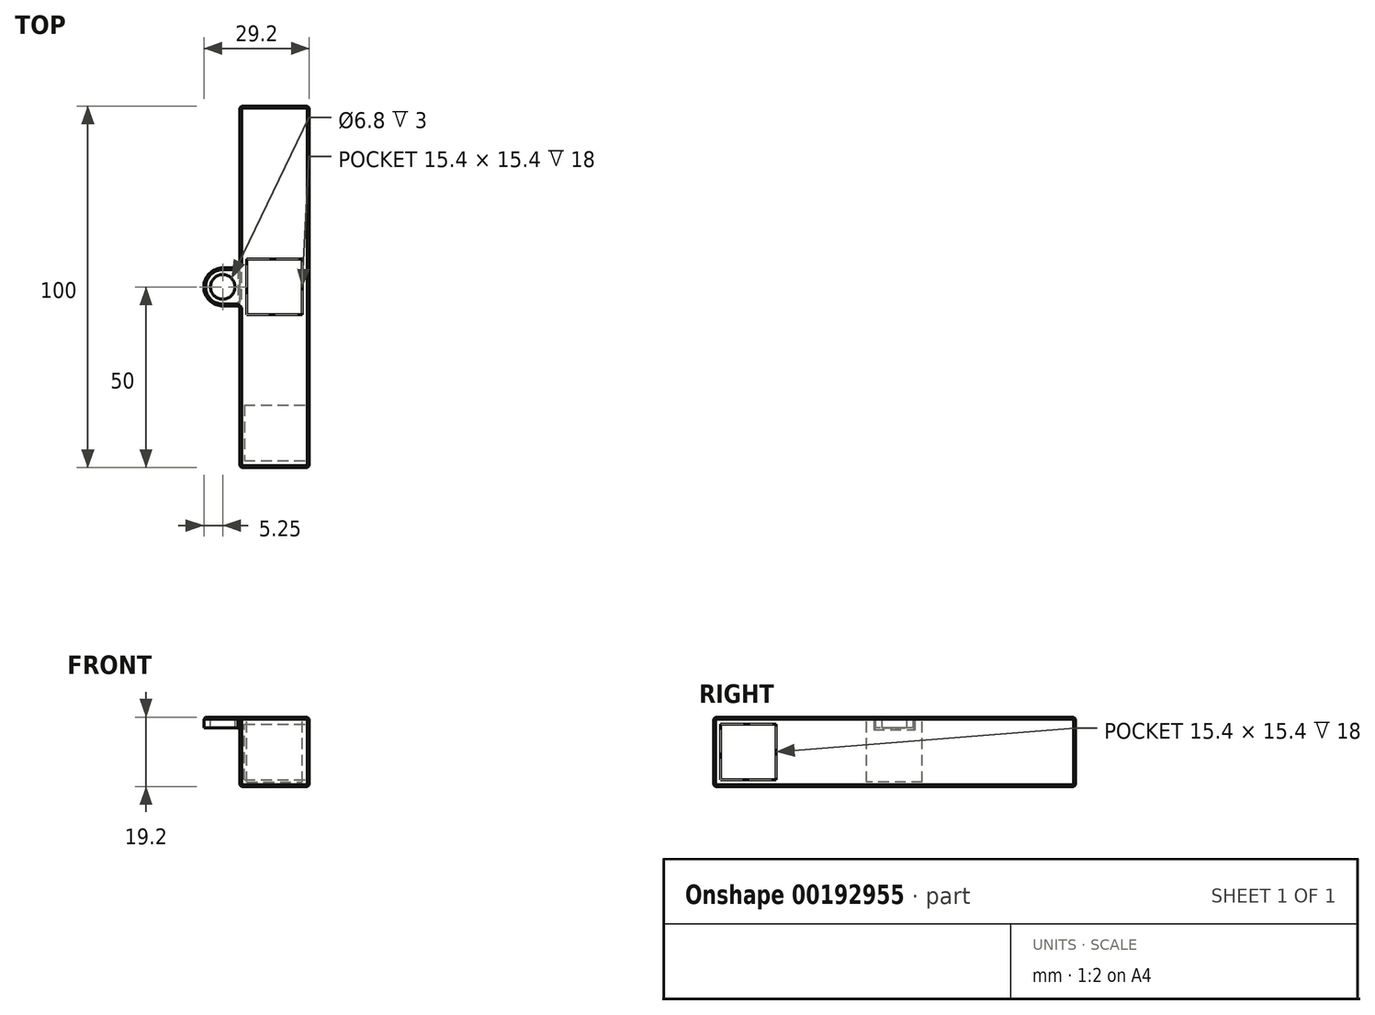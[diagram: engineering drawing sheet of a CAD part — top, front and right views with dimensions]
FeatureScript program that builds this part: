
annotation { "Feature Type Name" : "Feature", "Feature Type Description" : "" }
export const myFeature = defineFeature(function(context is Context, id is Id, definition is map)
    precondition{}
    {
        {
            var Q0;
            Q0=qCreatedBy(makeId("Top.planeOp"),FACE);
            var sketch = newSketch(context, id + "F0", { "sketchPlane" : qUnion([Q0])});
            skLineSegment(sketch, "E0.bottom", {"start": v(9.6, -50) * mm, "end": v(-9.6, -50) * mm});
            skLineSegment(sketch, "E0.top", {"start": v(9.6, 50) * mm, "end": v(-9.6, 50) * mm});
            skLineSegment(sketch, "E0.left", {"start": v(9.6, -50) * mm, "end": v(9.6, 50) * mm});
            skLineSegment(sketch, "E0.right", {"start": v(-9.6, -50) * mm, "end": v(-9.6, 50) * mm});
            skPoint(sketch, "E0.middle", {"position": v(0, 0) * mm});
            skSolve(sketch);
        }
        {
            var Q0;
            Q0=qSketchRegion(id+"F0",true);
            extrude(context, id + "F1", {"entities" : qUnion([Q0]), "depth" : 19.2 * mm});
        }
        {
            var Q0;
            Q0=makeQuery(id+"F1.opExtrude","SWEPT_FACE",FACE,{"disambiguationData":[OSD([sQuery(id+"F0.wireOp",EDGE,"E0.left")])]});
            var sketch = newSketch(context, id + "F2", { "sketchPlane" : qUnion([Q0])});
            skLineSegment(sketch, "E1.bottom", {"start": v(-32.7, 1.9) * mm, "end": v(-48.1, 1.9) * mm});
            skLineSegment(sketch, "E1.top", {"start": v(-32.7, 17.3) * mm, "end": v(-48.1, 17.3) * mm});
            skLineSegment(sketch, "E1.left", {"start": v(-32.7, 1.9) * mm, "end": v(-32.7, 17.3) * mm});
            skLineSegment(sketch, "E1.right", {"start": v(-48.1, 1.9) * mm, "end": v(-48.1, 17.3) * mm});
            skPoint(sketch, "E1.middle", {"position": v(-40.4, 9.6) * mm});
            skPoint(sketch, "E1.middle.positionSnap0", {"position": v(-50, 9.6) * mm});
            skPoint(sketch, "E1.centerSnap0", {"position": v(-50, 9.6) * mm});
            skSolve(sketch);
        }
        {
            var Q0;
            Q0=qSketchRegion(id+"F2",true);
            extrude(context, id + "F3", {"entities" : qUnion([Q0]), "operationType" : NewBodyOperationType.REMOVE, "oppositeDirection" : true, "depth" : 18 * mm});
        }
        {
            var Q0;
            Q0=makeQuery(id+"F1.opExtrude","CAP_FACE",FACE,{"disambiguationData":[OSD([sQuery(id+"F0.wireOp",EDGE,"E0.bottom"),sQuery(id+"F0.wireOp",EDGE,"E0.top"),sQuery(id+"F0.wireOp",EDGE,"E0.left"),sQuery(id+"F0.wireOp",EDGE,"E0.right")])],"isStart":false});
            var sketch = newSketch(context, id + "F4", { "sketchPlane" : qUnion([Q0])});
            skLineSegment(sketch, "E2.bottom", {"start": v(-19.6, 5.25) * mm, "end": v(0.4, 5.25) * mm});
            skLineSegment(sketch, "E2.top", {"start": v(-19.6, -5.25) * mm, "end": v(0.4, -5.25) * mm});
            skLineSegment(sketch, "E2.left", {"start": v(-19.6, 5.25) * mm, "end": v(-19.6, -5.25) * mm});
            skLineSegment(sketch, "E2.right", {"start": v(0.4, 5.25) * mm, "end": v(0.4, -5.25) * mm});
            skPoint(sketch, "E2.middle", {"position": v(-9.6, 0) * mm});
            skSolve(sketch);
        }
        {
            var Q0;
            Q0 = qSketchRegion(id + "F4", true);
            extrude(context, id + "F5", {"entities" : qUnion([Q0]), "operationType" : NewBodyOperationType.ADD, "oppositeDirection" : true, "depth" : 3 * mm});
        }
        {
            var Q0;
            Q0=makeQuery(id+"F5.opExtrude","SWEPT_EDGE",EDGE,{"disambiguationData":[OSD([sQuery(id+"F4.wireOp",EDGE,"E2.bottom"),sQuery(id+"F4.wireOp",EDGE,"E2.left")])]});
            var Q1;
            Q1=makeQuery(id+"F5.opExtrude","SWEPT_EDGE",EDGE,{"disambiguationData":[OSD([sQuery(id+"F4.wireOp",EDGE,"E2.top"),sQuery(id+"F4.wireOp",EDGE,"E2.left")])]});
            fillet(context, id + "F6", {"entities" : qUnion([Q0, Q1]), "radius" : 5.25 * mm, "tangentPropagation" : true, "allowEdgeOverflow" : false});
        }
        {
            var Q0;
            Q0=makeQuery(id+"F5.boolean.opBoolean","MERGE",FACE,{"derivedFrom":[makeQuery(id+"F1.opExtrude","CAP_FACE",FACE,{"disambiguationData":[OSD([sQuery(id+"F0.wireOp",EDGE,"E0.bottom"),sQuery(id+"F0.wireOp",EDGE,"E0.top"),sQuery(id+"F0.wireOp",EDGE,"E0.left"),sQuery(id+"F0.wireOp",EDGE,"E0.right")])],"isStart":false}),makeQuery(id+"F5.opExtrude","CAP_FACE",FACE,{"disambiguationData":[OSD([sQuery(id+"F4.wireOp",EDGE,"E2.bottom"),sQuery(id+"F4.wireOp",EDGE,"E2.top"),sQuery(id+"F4.wireOp",EDGE,"E2.left"),sQuery(id+"F4.wireOp",EDGE,"E2.right")])],"isStart":true})]});
            var sketch = newSketch(context, id + "F7", { "sketchPlane" : qUnion([Q0])});
            skCircle(sketch, "E3", {"center": v(-14.35, 0) * mm, "radius": 3.4 * mm});
            skSolve(sketch);
        }
        {
            var Q0;
            Q0 = qSketchRegion(id + "F7", true);
            extrude(context, id + "F8", {"entities" : qUnion([Q0]), "operationType" : NewBodyOperationType.REMOVE, "oppositeDirection" : true, "depth" : 25 * mm});
        }
        {
            var Q0;
            Q0=makeQuery(id+"F1.opExtrude","SWEPT_FACE",FACE,{"disambiguationData":[OSD([sQuery(id+"F0.wireOp",EDGE,"E0.right")])]});
            var Q1;
            Q1=makeQuery(id+"F1.opExtrude","SWEPT_FACE",FACE,{"disambiguationData":[OSD([sQuery(id+"F0.wireOp",EDGE,"E0.bottom")])]});
            var Q2;
            Q2=makeQuery(id+"F1.opExtrude","SWEPT_FACE",FACE,{"disambiguationData":[OSD([sQuery(id+"F0.wireOp",EDGE,"E0.top")])]});
            var Q3;
            Q3=makeQuery(id+"F1.opExtrude","CAP_FACE",FACE,{"disambiguationData":[OSD([sQuery(id+"F0.wireOp",EDGE,"E0.bottom"),sQuery(id+"F0.wireOp",EDGE,"E0.top"),sQuery(id+"F0.wireOp",EDGE,"E0.left"),sQuery(id+"F0.wireOp",EDGE,"E0.right")])],"isStart":true});
            var Q4;
            Q4=makeQuery(id+"F1.opExtrude","CAP_EDGE",EDGE,{"disambiguationData":[OSD([sQuery(id+"F0.wireOp",EDGE,"E0.left")])],"isStart":false});
            chamfer(context, id + "F9", {"entities" : qUnion([Q0, Q1, Q2, Q3, Q4]), "width" : 0.5 * mm, "tangentPropagation" : true});
        }
        {
            var Q0;
            Q0=makeQuery(id+"F1.opExtrude","CAP_FACE",FACE,{"disambiguationData":[OSD([sQuery(id+"F0.wireOp",EDGE,"E0.bottom"),sQuery(id+"F0.wireOp",EDGE,"E0.top"),sQuery(id+"F0.wireOp",EDGE,"E0.left"),sQuery(id+"F0.wireOp",EDGE,"E0.right")])],"isStart":false});
            var sketch = newSketch(context, id + "F10", { "sketchPlane" : qUnion([Q0])});
            skLineSegment(sketch, "E4.bottom", {"start": v(-7.7, -30.7) * mm, "end": v(7.7, -30.7) * mm});
            skLineSegment(sketch, "E4.top", {"start": v(-7.7, -15.3) * mm, "end": v(7.7, -15.3) * mm});
            skLineSegment(sketch, "E4.left", {"start": v(-7.7, -30.7) * mm, "end": v(-7.7, -15.3) * mm});
            skLineSegment(sketch, "E4.right", {"start": v(7.7, -30.7) * mm, "end": v(7.7, -15.3) * mm});
            skPoint(sketch, "E4.middle", {"position": v(0, -23) * mm});
            skPoint(sketch, "E4.middle.positionSnap0", {"position": v(0, -49.5) * mm});
            skPoint(sketch, "E4.centerSnap0", {"position": v(0, -49.5) * mm});
            skSolve(sketch);
        }
        {
            var Q0;
            Q0=makeQuery(id+"F10.imprint","IMPRINT",FACE,{"disambiguationData":[TD([[makeQuery(id+"F10.imprint","IMPRINT",EDGE,{"derivedFrom":sQuery(id+"F10.wireOp",EDGE,"E4.bottom")}),-1.0]])]});
            var sketch = newSketch(context, id + "F11", { "sketchPlane" : qUnion([Q0])});
            skLineSegment(sketch, "E5.bottom", {"start": v(-7.7, 7.7) * mm, "end": v(7.7, 7.7) * mm});
            skLineSegment(sketch, "E5.top", {"start": v(-7.7, -7.7) * mm, "end": v(7.7, -7.7) * mm});
            skLineSegment(sketch, "E5.left", {"start": v(-7.7, 7.7) * mm, "end": v(-7.7, -7.7) * mm});
            skLineSegment(sketch, "E5.right", {"start": v(7.7, 7.7) * mm, "end": v(7.7, -7.7) * mm});
            skPoint(sketch, "E5.middle", {"position": v(0, 0) * mm});
            skSolve(sketch);
        }
        {
            var Q0;
            Q0 = qSketchRegion(id + "F11", true);
            extrude(context, id + "F12", {"entities" : qUnion([Q0]), "operationType" : NewBodyOperationType.REMOVE, "oppositeDirection" : true, "depth" : 18 * mm});
        }
    });
